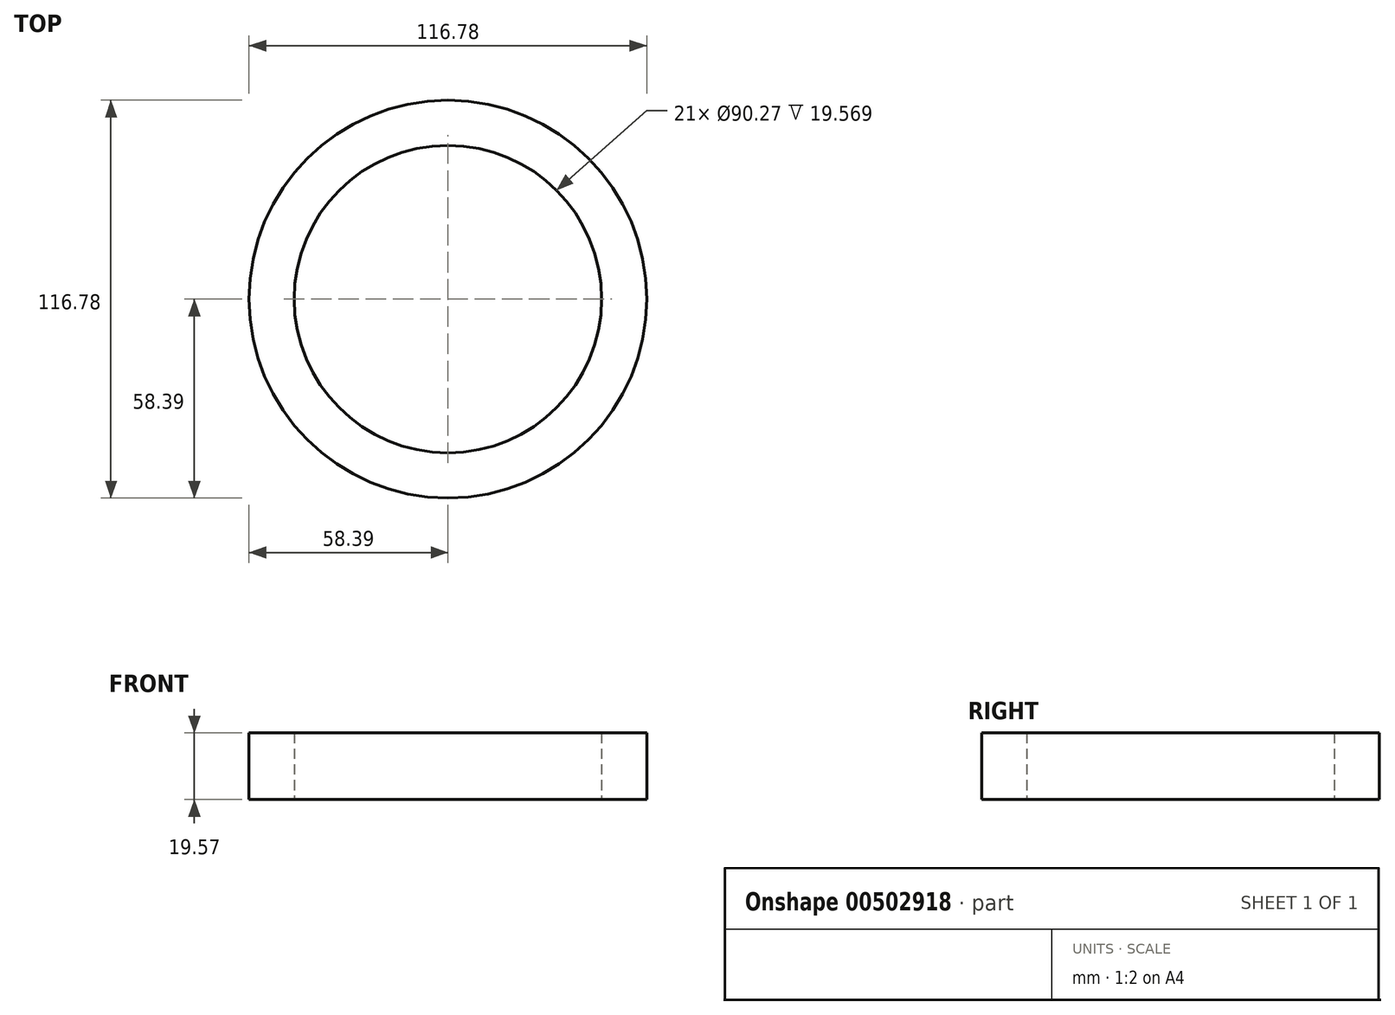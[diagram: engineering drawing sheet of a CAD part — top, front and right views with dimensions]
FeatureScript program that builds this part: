
annotation { "Feature Type Name" : "Feature", "Feature Type Description" : "" }
export const myFeature = defineFeature(function(context is Context, id is Id, definition is map)
    precondition{}
    {
        {
            var Q0;
            Q0=qCreatedBy(makeId("Front.planeOp"),FACE);
            var sketch = newSketch(context, id + "F0", { "sketchPlane" : qUnion([Q0])});
            skLineSegment(sketch, "E0.bottom", {"start": v(-45.13, 26.04) * mm, "end": v(-58.39, 26.04) * mm});
            skLineSegment(sketch, "E0.top", {"start": v(-45.13, 6.47) * mm, "end": v(-58.39, 6.47) * mm});
            skLineSegment(sketch, "E0.left", {"start": v(-45.13, 26.04) * mm, "end": v(-45.13, 6.47) * mm});
            skLineSegment(sketch, "E0.right", {"start": v(-58.39, 26.04) * mm, "end": v(-58.39, 6.47) * mm});
            skPoint(sketch, "E0.middle", {"position": v(-51.76, 16.25) * mm});
            skLineSegment(sketch, "E1", {"start": v(0, 0) * mm, "end": v(0, 49.08) * mm, "construction": true});
            skLineSegment(sketch, "E2", {"start": v(0, 0) * mm, "end": v(46.4, 0) * mm, "construction": true});
            skLineSegment(sketch, "E3", {"start": v(0, 0) * mm, "end": v(0, -35.82) * mm, "construction": true});
            skSolve(sketch);
        }
        {
            var Q0;
            Q0 = qSketchRegion(id + "F0", true);
            var Q1;
            Q1=sQuery(id+"F0.wireOp",EDGE,"E1");
            revolve(context, id + "F1", {"entities" : qUnion([Q0]), "axis" : qUnion([Q1]), "revolveType" : RevolveType.FULL});
        }
    });
